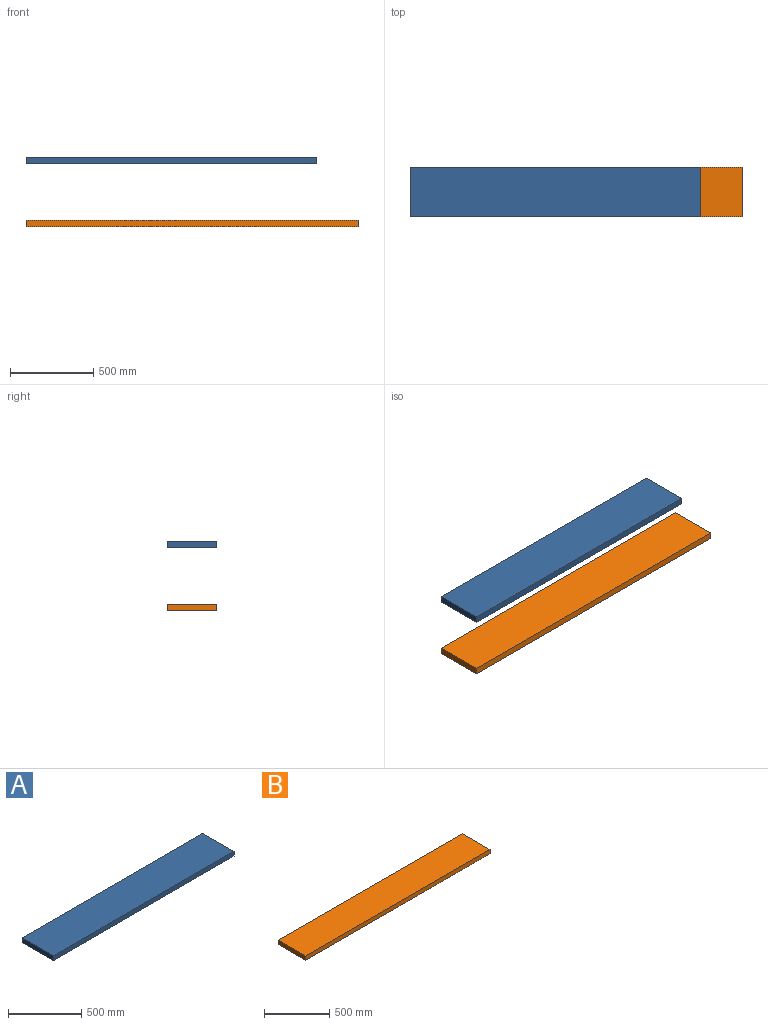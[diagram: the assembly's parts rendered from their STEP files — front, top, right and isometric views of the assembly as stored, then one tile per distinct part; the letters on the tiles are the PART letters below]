
ASSEMBLY  parts=2 mates=2
PART A: 6 faces, bbox 1750x300x40 mm
  f0: plane 1750x300mm, normal (0,0,1), area 525000mm2, adj f1,f3,f4,f5
  f1: plane 300x40mm, normal (-1,0,0), area 12000mm2, adj f0,f2,f4,f5
  f2: plane 1750x300mm, normal (0,0,-1), area 525000mm2, adj f1,f3,f4,f5
  f3: plane 300x40mm, normal (1,0,0), area 12000mm2, adj f0,f2,f4,f5
  f4: plane 1750x40mm, normal (0,1,0), area 70000mm2, adj f0,f1,f2,f3
  f5: plane 1750x40mm, normal (0,-1,0), area 70000mm2, adj f0,f1,f2,f3
PART B: 6 faces, bbox 2000x300x40 mm
  f0: plane 2000x300mm, normal (0,0,1), area 600000mm2, adj f1,f3,f4,f5
  f1: plane 300x40mm, normal (-1,0,0), area 12000mm2, adj f0,f2,f4,f5
  f2: plane 2000x300mm, normal (0,0,-1), area 600000mm2, adj f1,f3,f4,f5
  f3: plane 300x40mm, normal (1,0,0), area 12000mm2, adj f0,f2,f4,f5
  f4: plane 2000x40mm, normal (0,1,0), area 80000mm2, adj f0,f1,f2,f3
  f5: plane 2000x40mm, normal (0,-1,0), area 80000mm2, adj f0,f1,f2,f3
PLACE A t=(-113.76,339.53,792.8)mm
PLACE B t=(11.24,339.53,412.8)mm
MATE parallel A.f0 <-> B.f2  axis (0,0,1) through (-113.76,489.53,812.8)mm
MATE planar B.f1 <-> A.f1  axis (-1,0,0) through (-988.76,489.53,412.8)mm
